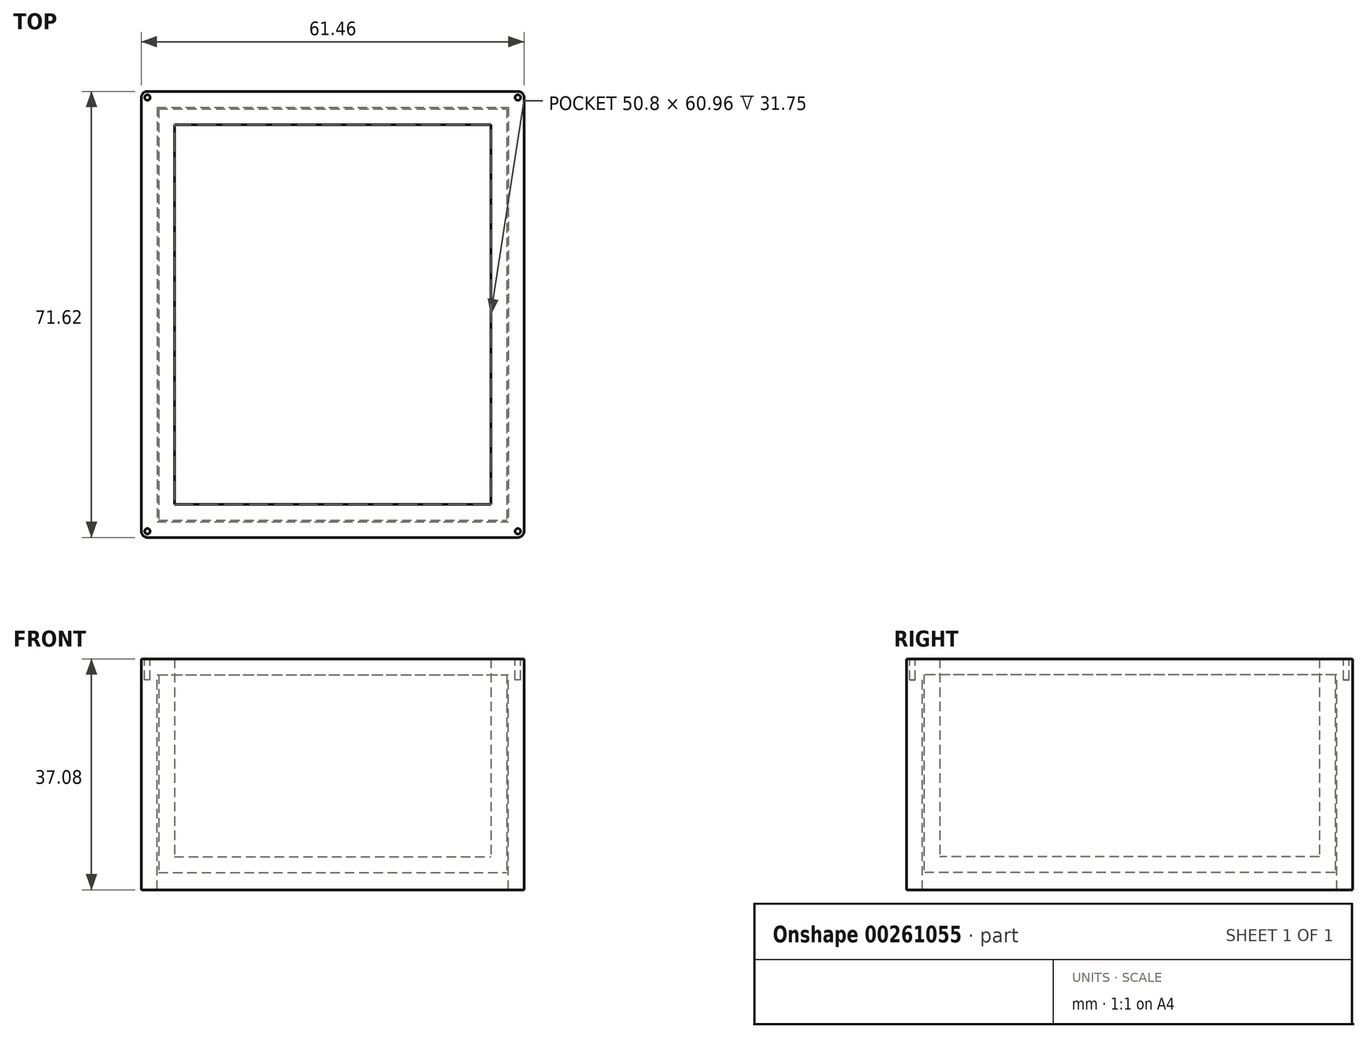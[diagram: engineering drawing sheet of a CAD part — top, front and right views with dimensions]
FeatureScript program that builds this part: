
annotation { "Feature Type Name" : "Feature", "Feature Type Description" : "" }
export const myFeature = defineFeature(function(context is Context, id is Id, definition is map)
    precondition{}
    {
        {
            var Q0;
            Q0=qCreatedBy(makeId("Top.planeOp"),FACE);
            var sketch = newSketch(context, id + "F0", { "sketchPlane" : qUnion([Q0])});
            skPoint(sketch, "E0.middle", {"position": v(0, 0) * mm});
            skLineSegment(sketch, "E1.bottom", {"start": v(-25.4, 30.48) * mm, "end": v(25.4, 30.48) * mm});
            skLineSegment(sketch, "E1.top", {"start": v(-25.4, -30.48) * mm, "end": v(25.4, -30.48) * mm});
            skLineSegment(sketch, "E1.left", {"start": v(-25.4, 30.48) * mm, "end": v(-25.4, -30.48) * mm});
            skLineSegment(sketch, "E1.right", {"start": v(25.4, 30.48) * mm, "end": v(25.4, -30.48) * mm});
            skPoint(sketch, "E2.start.orphan", {"position": v(-30.73, 35.81) * mm});
            skPoint(sketch, "E0.right.start.orphan", {"position": v(-30.73, 31.75) * mm});
            skPoint(sketch, "E3.end.orphan", {"position": v(-30.73, -31.75) * mm});
            skPoint(sketch, "E4.end.orphan", {"position": v(-30.73, -35.81) * mm});
            skPoint(sketch, "E5.end.orphan", {"position": v(30.73, -35.81) * mm});
            skPoint(sketch, "E0.left.end.orphan", {"position": v(30.73, -31.75) * mm});
            skPoint(sketch, "E6.end.orphan", {"position": v(26.67, 35.81) * mm});
            skPoint(sketch, "E7.end.orphan", {"position": v(30.73, 35.81) * mm});
            skLineSegment(sketch, "E8.bottom", {"start": v(-30.73, 35.81) * mm, "end": v(30.73, 35.81) * mm});
            skLineSegment(sketch, "E8.top", {"start": v(-30.73, -35.81) * mm, "end": v(30.73, -35.81) * mm});
            skLineSegment(sketch, "E8.left", {"start": v(-30.73, 35.81) * mm, "end": v(-30.73, -35.81) * mm});
            skLineSegment(sketch, "E8.right", {"start": v(30.73, 35.81) * mm, "end": v(30.73, -35.81) * mm});
            skSolve(sketch);
        }
        {
            var Q0;
            Q0=makeQuery(id+"F0.imprint","IMPRINT",FACE,{"disambiguationData":[TD([[makeQuery(id+"F0.imprint","IMPRINT",EDGE,{"derivedFrom":sQuery(id+"F0.wireOp",EDGE,"E1.bottom")}),1.0]])]});
            extrude(context, id + "F1", {"entities" : qUnion([Q0]), "endBound" : BoundingType.SYMMETRIC, "depth" : 37.08 * mm});
        }
        {
            var Q0;
            Q0=makeQuery(id+"F1.opExtrude","CAP_FACE",FACE,{"disambiguationData":[OSD([sQuery(id+"F0.wireOp",EDGE,"E1.bottom"),sQuery(id+"F0.wireOp",EDGE,"E1.top"),sQuery(id+"F0.wireOp",EDGE,"E1.left"),sQuery(id+"F0.wireOp",EDGE,"E1.right"),sQuery(id+"F0.wireOp",EDGE,"E8.bottom"),sQuery(id+"F0.wireOp",EDGE,"E8.top"),sQuery(id+"F0.wireOp",EDGE,"E8.left"),sQuery(id+"F0.wireOp",EDGE,"E8.right")])],"isStart":true});
            var sketch = newSketch(context, id + "F2", { "sketchPlane" : qUnion([Q0])});
            skLineSegment(sketch, "E9.bottom", {"start": v(-25.4, 30.48) * mm, "end": v(25.4, 30.48) * mm});
            skLineSegment(sketch, "E9.top", {"start": v(-25.4, -30.48) * mm, "end": v(25.4, -30.48) * mm});
            skLineSegment(sketch, "E9.left", {"start": v(-25.4, 30.48) * mm, "end": v(-25.4, -30.48) * mm});
            skLineSegment(sketch, "E9.right", {"start": v(25.4, 30.48) * mm, "end": v(25.4, -30.48) * mm});
            skSolve(sketch);
        }
        {
            var Q0;
            Q0 = qSketchRegion(id + "F2", true);
            extrude(context, id + "F3", {"entities" : qUnion([Q0]), "operationType" : NewBodyOperationType.ADD, "oppositeDirection" : true, "depth" : 5.33 * mm});
        }
        {
            var Q0;
            Q0=makeQuery(id+"F1.opExtrude","SWEPT_EDGE",EDGE,{"disambiguationData":[OSD([sQuery(id+"F0.wireOp",EDGE,"E8.bottom"),sQuery(id+"F0.wireOp",EDGE,"E8.left")])]});
            var Q1;
            Q1=makeQuery(id+"F1.opExtrude","SWEPT_EDGE",EDGE,{"disambiguationData":[OSD([sQuery(id+"F0.wireOp",EDGE,"E8.bottom"),sQuery(id+"F0.wireOp",EDGE,"E8.right")])]});
            var Q2;
            Q2=makeQuery(id+"F1.opExtrude","SWEPT_EDGE",EDGE,{"disambiguationData":[OSD([sQuery(id+"F0.wireOp",EDGE,"E8.top"),sQuery(id+"F0.wireOp",EDGE,"E8.right")])]});
            var Q3;
            Q3=makeQuery(id+"F1.opExtrude","SWEPT_EDGE",EDGE,{"disambiguationData":[OSD([sQuery(id+"F0.wireOp",EDGE,"E8.top"),sQuery(id+"F0.wireOp",EDGE,"E8.left")])]});
            fillet(context, id + "F4", {"entities" : qUnion([Q0, Q1, Q2, Q3]), "radius" : 1 * mm, "tangentPropagation" : true, "allowEdgeOverflow" : false});
        }
        {
            var Q0;
            Q0=makeQuery(id+"F3.boolean.opBoolean","MERGE",FACE,{"derivedFrom":[makeQuery(id+"F1.opExtrude","CAP_FACE",FACE,{"disambiguationData":[OSD([sQuery(id+"F0.wireOp",EDGE,"E1.bottom"),sQuery(id+"F0.wireOp",EDGE,"E1.top"),sQuery(id+"F0.wireOp",EDGE,"E1.left"),sQuery(id+"F0.wireOp",EDGE,"E1.right"),sQuery(id+"F0.wireOp",EDGE,"E8.bottom"),sQuery(id+"F0.wireOp",EDGE,"E8.top"),sQuery(id+"F0.wireOp",EDGE,"E8.left"),sQuery(id+"F0.wireOp",EDGE,"E8.right")])],"isStart":true}),makeQuery(id+"F3.opExtrude","CAP_FACE",FACE,{"disambiguationData":[OSD([sQuery(id+"F2.wireOp",EDGE,"E9.bottom"),sQuery(id+"F2.wireOp",EDGE,"E9.top"),sQuery(id+"F2.wireOp",EDGE,"E9.left"),sQuery(id+"F2.wireOp",EDGE,"E9.right")])],"isStart":true})]});
            shell(context, id + "F5", {"entities" : qUnion([Q0]), "thickness" : 2.54 * mm});
        }
        {
            var Q0;
            Q0=makeQuery(id+"F1.opExtrude","CAP_FACE",FACE,{"disambiguationData":[OSD([sQuery(id+"F0.wireOp",EDGE,"E1.bottom"),sQuery(id+"F0.wireOp",EDGE,"E1.top"),sQuery(id+"F0.wireOp",EDGE,"E1.left"),sQuery(id+"F0.wireOp",EDGE,"E1.right"),sQuery(id+"F0.wireOp",EDGE,"E8.bottom"),sQuery(id+"F0.wireOp",EDGE,"E8.top"),sQuery(id+"F0.wireOp",EDGE,"E8.left"),sQuery(id+"F0.wireOp",EDGE,"E8.right")])],"isStart":false});
            var sketch = newSketch(context, id + "F6", { "sketchPlane" : qUnion([Q0])});
            skCircle(sketch, "E10", {"center": v(-29.74, 34.82) * mm, "radius": 0.44 * mm});
            skCircle(sketch, "E11", {"center": v(29.74, 34.82) * mm, "radius": 0.44 * mm});
            skCircle(sketch, "E12", {"center": v(29.74, -34.82) * mm, "radius": 0.44 * mm});
            skCircle(sketch, "E13", {"center": v(-29.74, -34.82) * mm, "radius": 0.44 * mm});
            skSolve(sketch);
        }
        {
            var Q0;
            Q0=makeQuery(id+"F6.imprint","IMPRINT",FACE,{"disambiguationData":[TD([[makeQuery(id+"F6.imprint","IMPRINT",EDGE,{"derivedFrom":sQuery(id+"F6.wireOp",EDGE,"E10")}),1.0]])]});
            var Q1;
            Q1=makeQuery(id+"F6.imprint","IMPRINT",FACE,{"disambiguationData":[TD([[makeQuery(id+"F6.imprint","IMPRINT",EDGE,{"derivedFrom":sQuery(id+"F6.wireOp",EDGE,"E11")}),1.0]])]});
            var Q2;
            Q2=makeQuery(id+"F6.imprint","IMPRINT",FACE,{"disambiguationData":[TD([[makeQuery(id+"F6.imprint","IMPRINT",EDGE,{"derivedFrom":sQuery(id+"F6.wireOp",EDGE,"E12")}),1.0]])]});
            var Q3;
            Q3=makeQuery(id+"F6.imprint","IMPRINT",FACE,{"disambiguationData":[TD([[makeQuery(id+"F6.imprint","IMPRINT",EDGE,{"derivedFrom":sQuery(id+"F6.wireOp",EDGE,"E13")}),1.0]])]});
            extrude(context, id + "F7", {"entities" : qUnion([Q0, Q1, Q2, Q3]), "operationType" : NewBodyOperationType.REMOVE, "oppositeDirection" : true, "depth" : 3.38 * mm});
        }
    });
